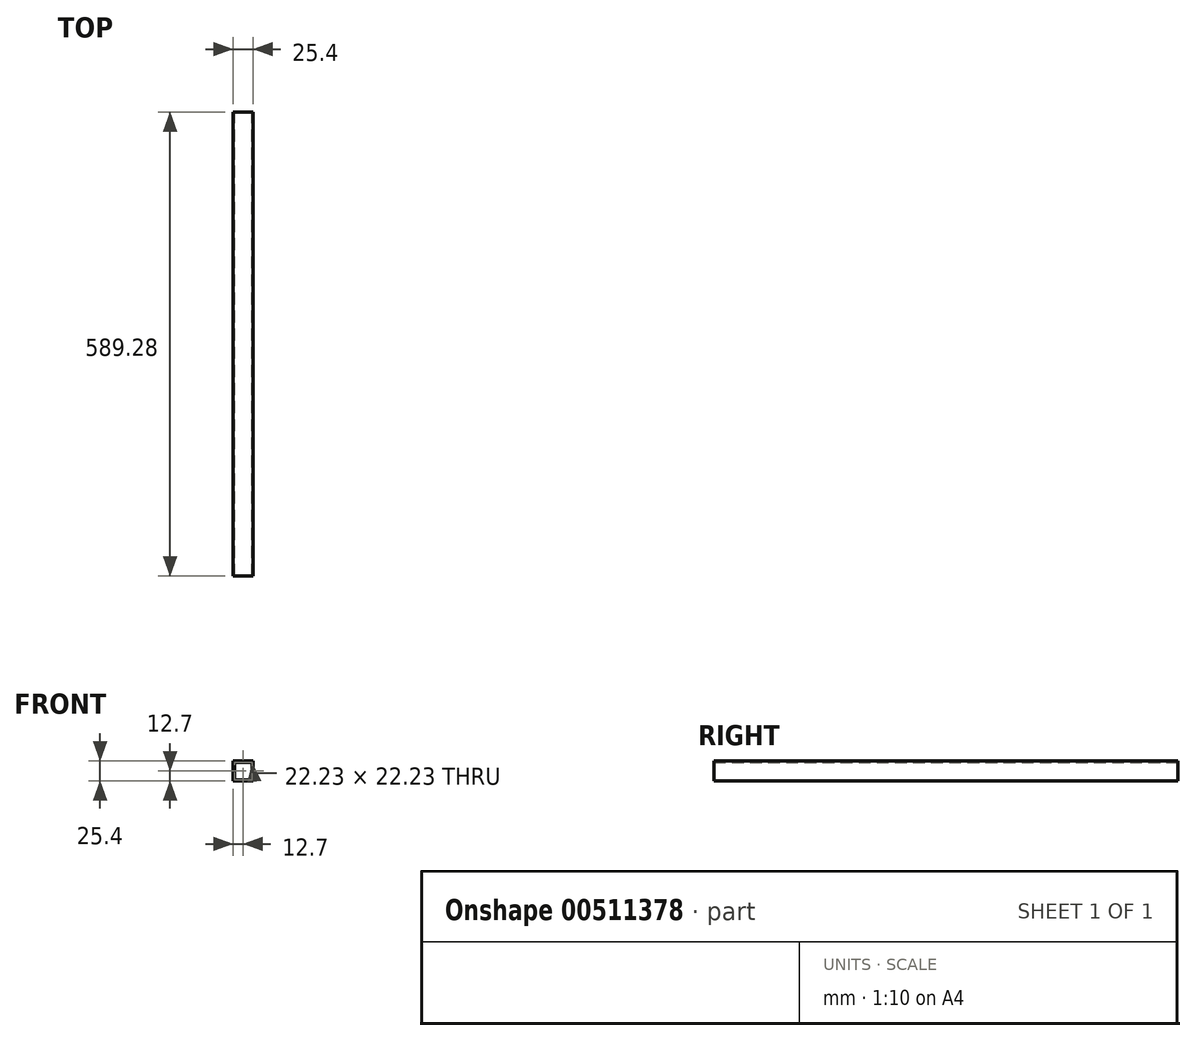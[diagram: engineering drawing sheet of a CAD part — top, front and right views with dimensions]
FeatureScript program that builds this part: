
annotation { "Feature Type Name" : "Feature", "Feature Type Description" : "" }
export const myFeature = defineFeature(function(context is Context, id is Id, definition is map)
    precondition{}
    {
        {
            var Q0;
            Q0=qCreatedBy(makeId("Front.planeOp"),FACE);
            var sketch = newSketch(context, id + "F0", { "sketchPlane" : qUnion([Q0])});
            skLineSegment(sketch, "E0.bottom", {"start": v(-12.7, 12.7) * mm, "end": v(12.7, 12.7) * mm});
            skLineSegment(sketch, "E0.top", {"start": v(-12.7, -12.7) * mm, "end": v(12.7, -12.7) * mm});
            skLineSegment(sketch, "E0.left", {"start": v(-12.7, 12.7) * mm, "end": v(-12.7, -12.7) * mm});
            skLineSegment(sketch, "E0.right", {"start": v(12.7, 12.7) * mm, "end": v(12.7, -12.7) * mm});
            skPoint(sketch, "E0.middle", {"position": v(0, 0) * mm});
            skLineSegment(sketch, "E1.bottom", {"start": v(-11.11, 11.11) * mm, "end": v(11.11, 11.11) * mm});
            skLineSegment(sketch, "E1.top", {"start": v(-11.11, -11.11) * mm, "end": v(11.11, -11.11) * mm});
            skLineSegment(sketch, "E1.left", {"start": v(-11.11, 11.11) * mm, "end": v(-11.11, -11.11) * mm});
            skLineSegment(sketch, "E1.right", {"start": v(11.11, 11.11) * mm, "end": v(11.11, -11.11) * mm});
            skSolve(sketch);
        }
        {
            var Q0;
            Q0=makeQuery(id+"F0.imprint","IMPRINT",FACE,{"disambiguationData":[TD([[makeQuery(id+"F0.imprint","IMPRINT",EDGE,{"derivedFrom":sQuery(id+"F0.wireOp",EDGE,"E0.bottom")}),-1.0]])]});
            extrude(context, id + "F1", {"entities" : qUnion([Q0]), "endBound" : BoundingType.SYMMETRIC, "depth" : 589.28 * mm, "offsetDistance" : 25.4 * mm});
        }
    });
